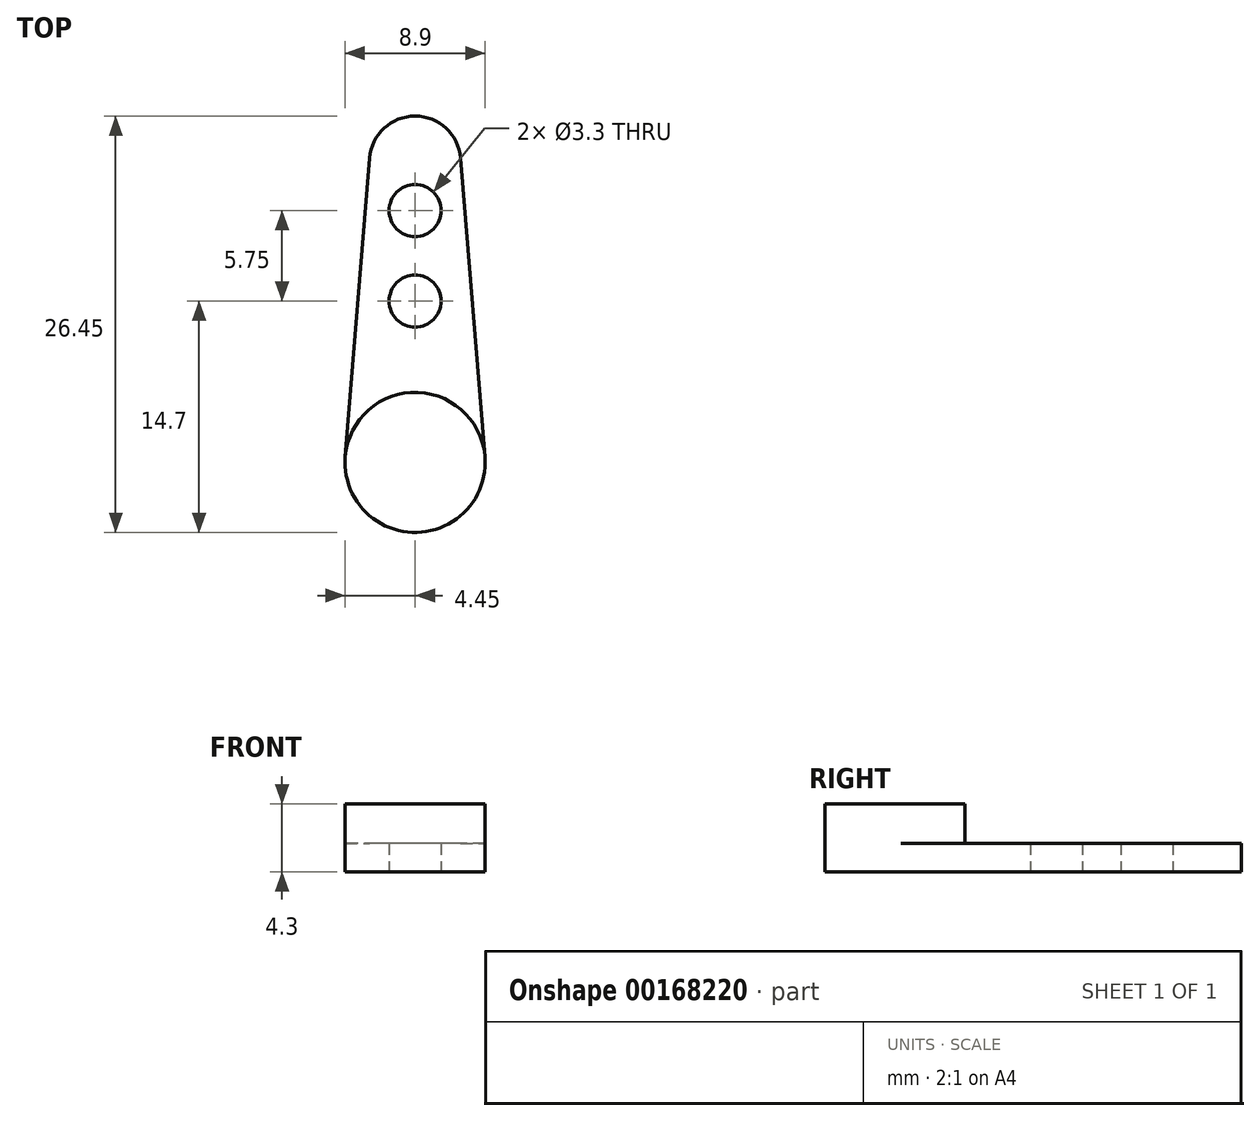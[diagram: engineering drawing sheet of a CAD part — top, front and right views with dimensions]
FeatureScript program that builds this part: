
annotation { "Feature Type Name" : "Feature", "Feature Type Description" : "" }
export const myFeature = defineFeature(function(context is Context, id is Id, definition is map)
    precondition{}
    {
        {
            var Q0;
            Q0=qCreatedBy(makeId("Top.planeOp"),FACE);
            var sketch = newSketch(context, id + "F0", { "sketchPlane" : qUnion([Q0])});
            skCircle(sketch, "E0", {"center": v(0, 0) * mm, "radius": 4.45 * mm});
            skLineSegment(sketch, "E1", {"start": v(0, 0) * mm, "end": v(0, 19.34) * mm, "construction": true});
            skLineSegment(sketch, "E2", {"start": v(-2.9, 19.34) * mm, "end": v(2.9, 19.34) * mm, "construction": true});
            skLineSegment(sketch, "E3", {"start": v(-4.44, 0.36) * mm, "end": v(-2.9, 19.34) * mm});
            skLineSegment(sketch, "E4", {"start": v(2.9, 19.34) * mm, "end": v(4.44, 0.36) * mm});
            skArc(sketch, "E5", {"start": v(-2.9, 19.34) * mm, "mid": v(0, 22) * mm, "end": v(2.9, 19.34) * mm});
            skSolve(sketch);
        }
        {
            var Q0;
            {var subQ0=sQuery(id+"F0.wireOp",EDGE,"E3");Q0=makeQuery(id+"F0.imprint","IMPRINT",FACE,{"disambiguationData":[TD([[makeQuery(id+"F0.imprint","IMPRINT",EDGE,{"derivedFrom":subQ0}),-1.0]])]});}
            var Q1;
            {var subQ0=sQuery(id+"F0.wireOp",EDGE,"E0");var subQ1=makeQuery(id+"F0.imprint","INTERSECT",VERTEX,{"derivedFrom":[subQ0,sQuery(id+"F0.wireOp",EDGE,"E3")]});Q1=makeQuery(id+"F0.imprint","IMPRINT",FACE,{"disambiguationData":[TD([[makeQuery(id+"F0.imprint","IMPRINT",EDGE,{"disambiguationData":[TD([[subQ1,1.0]])],"derivedFrom":subQ0}),1.0]])]});}
            extrude(context, id + "F1", {"entities" : qUnion([Q0, Q1]), "depth" : 1.81 * mm, "offsetDistance" : 25 * mm});
        }
        {
            var Q0;
            {var subQ0=sQuery(id+"F0.wireOp",EDGE,"E0");var subQ1=makeQuery(id+"F0.imprint","INTERSECT",VERTEX,{"derivedFrom":[subQ0,sQuery(id+"F0.wireOp",EDGE,"E3")]});Q0=makeQuery(id+"F0.imprint","IMPRINT",FACE,{"disambiguationData":[TD([[makeQuery(id+"F0.imprint","IMPRINT",EDGE,{"disambiguationData":[TD([[subQ1,1.0]])],"derivedFrom":subQ0}),1.0]])]});}
            extrude(context, id + "F2", {"entities" : qUnion([Q0]), "operationType" : NewBodyOperationType.ADD, "depth" : 4.3 * mm, "offsetDistance" : 25 * mm});
        }
        {
            var Q0;
            Q0=makeQuery(id+"F1.opExtrude","CAP_FACE",FACE,{"disambiguationData":[OSD([sQuery(id+"F0.wireOp",EDGE,"E0"),sQuery(id+"F0.wireOp",EDGE,"E3"),sQuery(id+"F0.wireOp",EDGE,"E4"),sQuery(id+"F0.wireOp",EDGE,"E5")])],"isStart":true});
            var sketch = newSketch(context, id + "F3", { "sketchPlane" : qUnion([Q0])});
            skLineSegment(sketch, "E6", {"start": v(0, -10.25) * mm, "end": v(0, -16) * mm, "construction": true});
            skSolve(sketch);
        }
        {
            var Q0;
            Q0=sQuery(id+"F3.wireOp",VERTEX,"E6.start");
            var Q1;
            Q1=sQuery(id+"F3.wireOp",VERTEX,"E6.end");
            var Q2;
            Q2=makeQuery(id+"F1.opExtrude","SWEPT_BODY",BODY,{"disambiguationData":[OSD([sQuery(id+"F0.wireOp",EDGE,"E0"),sQuery(id+"F0.wireOp",EDGE,"E3"),sQuery(id+"F0.wireOp",EDGE,"E4"),sQuery(id+"F0.wireOp",EDGE,"E5")])]});
            hole(context, id + "F4", {"style" : HoleStyle.SIMPLE, "endStyle" : HoleEndStyle.THROUGH, "standardTappedOrClearance" : lookupTablePath({ "standard" : "ISO", "fit" : "Normal", "size" : "M3", "type" : "Clearance" }), "standardBlindInLast" : lookupTablePath({ "fit" : "Standard", "standard" : "ISO", "size" : "M3", "type" : "Clearance" }), "holeDiameter" : 3.3 * mm, "majorDiameter" : 3 * mm, "isTappedThrough" : true, "tappedDepth" : 12 * mm, "tapClearance" : 3, "locations" : qUnion([Q0, Q1]), "scope" : qUnion([Q2])});
        }
    });
